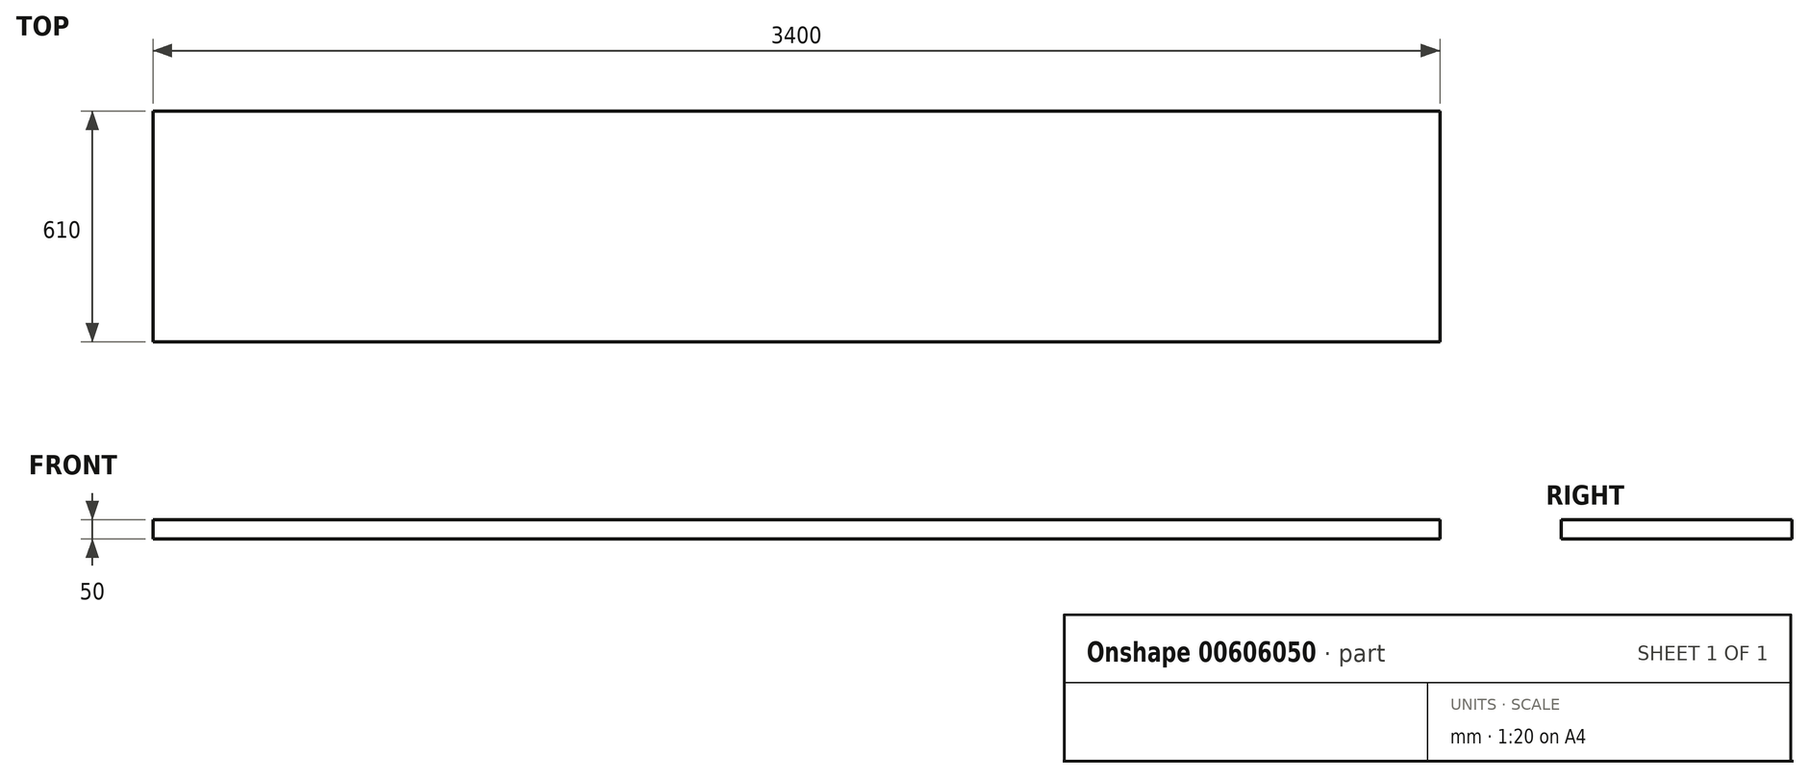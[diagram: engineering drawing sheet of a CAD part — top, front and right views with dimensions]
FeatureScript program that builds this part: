
annotation { "Feature Type Name" : "Feature", "Feature Type Description" : "" }
export const myFeature = defineFeature(function(context is Context, id is Id, definition is map)
    precondition{}
    {
        {
            var Q0;
            Q0=qCreatedBy(makeId("Top.planeOp"),FACE);
            var sketch = newSketch(context, id + "F0", { "sketchPlane" : qUnion([Q0])});
            skLineSegment(sketch, "E0.bottom", {"start": v(1700, 305) * mm, "end": v(-1700, 305) * mm});
            skLineSegment(sketch, "E0.top", {"start": v(1700, -305) * mm, "end": v(-1700, -305) * mm});
            skLineSegment(sketch, "E0.left", {"start": v(1700, 305) * mm, "end": v(1700, -305) * mm});
            skLineSegment(sketch, "E0.right", {"start": v(-1700, 305) * mm, "end": v(-1700, -305) * mm});
            skPoint(sketch, "E0.middle", {"position": v(0, 0) * mm});
            skSolve(sketch);
        }
        {
            var Q0;
            Q0=makeQuery(id+"F0.imprint","IMPRINT",FACE,{"disambiguationData":[TD([[makeQuery(id+"F0.imprint","IMPRINT",EDGE,{"derivedFrom":sQuery(id+"F0.wireOp",EDGE,"E0.bottom")}),1.0]])]});
            extrude(context, id + "F1", {"entities" : qUnion([Q0]), "depth" : 50 * mm, "offsetDistance" : 25 * mm});
        }
    });
